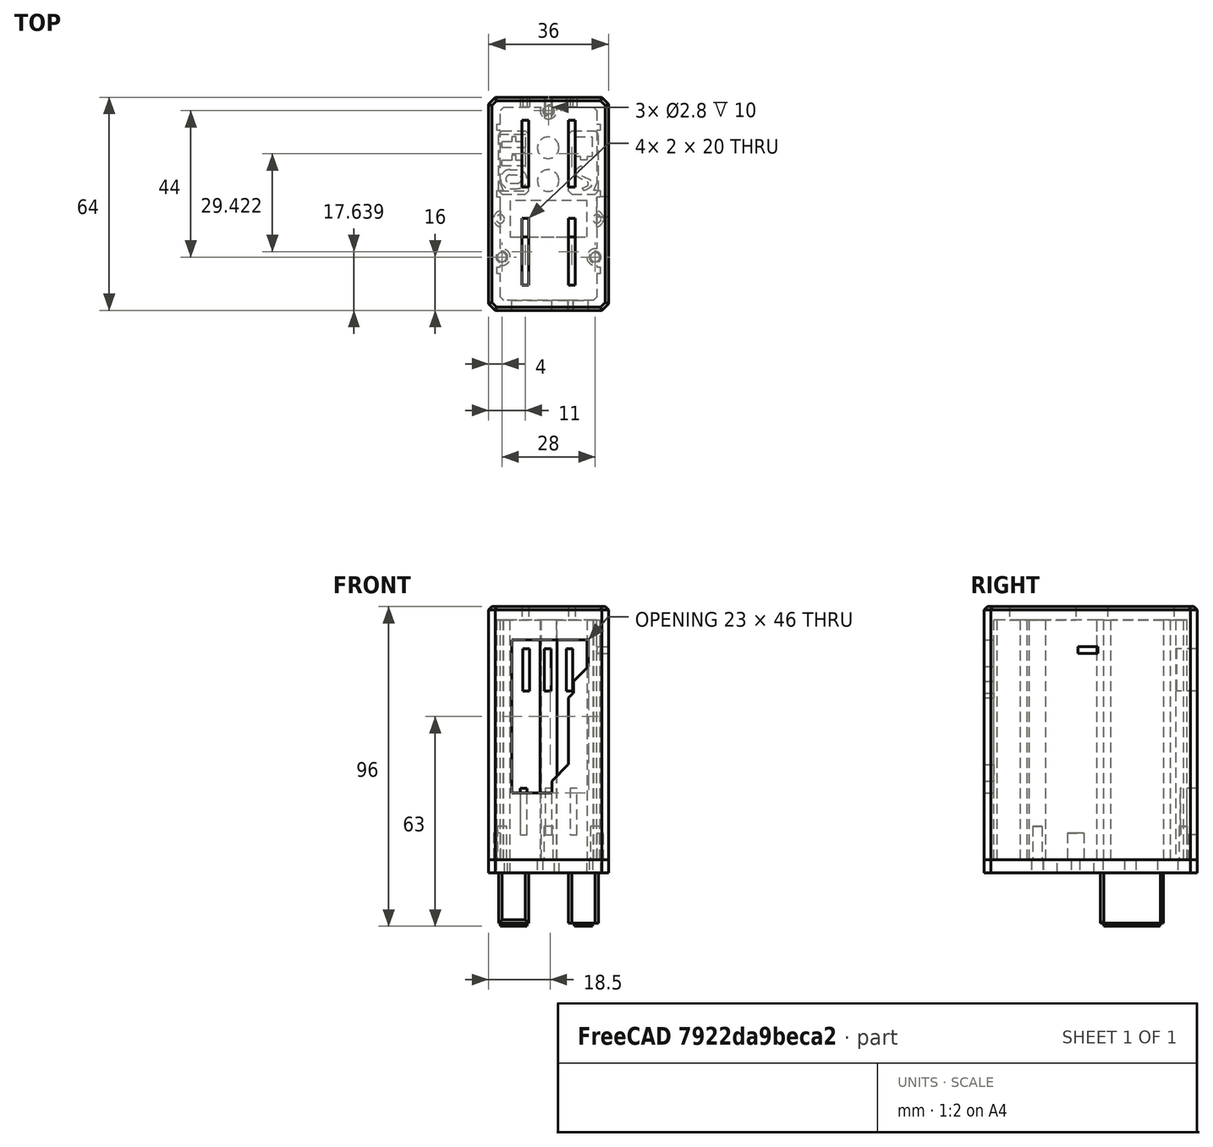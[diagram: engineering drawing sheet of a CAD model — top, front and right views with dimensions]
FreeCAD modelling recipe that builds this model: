
FCSTD DOCUMENT  (FreeCAD 0.19R)
Label: SwitchBox1
License: All rights reserved
LicenseURL: http://en.wikipedia.org/wiki/All_rights_reserved
objects: Sketcher::SketchObject×19, PartDesign::Pocket×11, PartDesign::Chamfer×9, PartDesign::Pad×8, PartDesign::Mirrored×2, PartDesign::Body×2, PartDesign::LinearPattern×1, PartDesign::Fillet×1, Mesh::Feature×1
note: 82 computed .brp shape members not serialized (recipe doc carries the construction recipe); baked Part::Feature solids carry a one-line shape summary decoded from their .brp

FEATURE [Sketcher::SketchObject] Sketch003
  FullyConstrained = true
  MapMode = 5
  Support = -> [XY_Plane001]
  sketch-geometry (4):
    g0: LineSegment StartX=-18 StartY=32 StartZ=0 EndX=18 EndY=32 EndZ=0
    g1: LineSegment StartX=18 StartY=32 StartZ=0 EndX=18 EndY=-32 EndZ=0
    g2: LineSegment StartX=18 StartY=-32 StartZ=0 EndX=-18 EndY=-32 EndZ=0
    g3: LineSegment StartX=-18 StartY=-32 StartZ=0 EndX=-18 EndY=32 EndZ=0
  constraints (10):
    c: Coincident(g0,g1)
    c: Coincident(g1,g2)
    c: Coincident(g2,g3)
    c: Coincident(g3,g0)
    c: Horizontal(g2)
    c: Vertical(g3)
    c: Distance(g0) = 36
    c: Distance(g1) = 64
    c: Symmetric(g0,g1,g-1)
    c: Symmetric(g0,g0,g-2)
FEATURE [PartDesign::Pad] Pad005
  Direction = (1,1,1)
  Length = 4
  Length2 = 100
  Profile = -> Sketch003
  Type = 0
FEATURE [Sketcher::SketchObject] Sketch005
  FullyConstrained = false
  MapMode = 5
  Placement = pos=(0,0,0) rot=(1,0,0;3.14159rad)
  Support = -> [Pad005]
  sketch-geometry (2):
    g0: Circle CenterX=-0.128096 CenterY=-16.8565 CenterZ=0 NormalX=0 NormalY=0 NormalZ=1 AngleXU=0 Radius=3.25
    g1: Circle CenterX=-0.128096 CenterY=-6.99288 CenterZ=0 NormalX=0 NormalY=0 NormalZ=1 AngleXU=0 Radius=3.25
  constraints (2):
    c: Diameter(g1) = 6.5
    c: Diameter(g0) = 6.5
FEATURE [PartDesign::Pocket] Pocket001
  BaseFeature = -> Pad005
  Length = 5
  Length2 = 100
  Profile = -> Sketch005
  Type = 0
FEATURE [Sketcher::SketchObject] Sketch006
  FullyConstrained = false
  MapMode = 5
  Placement = pos=(0,0,0) rot=(1,0,0;3.14159rad)
  Support = -> [Pocket001]
  sketch-geometry (8):
    g0: LineSegment StartX=-15 StartY=-2.91162 StartZ=0 EndX=-15 EndY=-21.9362 EndZ=0
    g1: LineSegment StartX=15 StartY=-2.91162 StartZ=0 EndX=15 EndY=-21.9362 EndZ=0
    g2: LineSegment StartX=-6 StartY=-2.91162 StartZ=0 EndX=-6 EndY=-21.9362 EndZ=0
    g3: LineSegment StartX=6 StartY=-2.91162 StartZ=0 EndX=6 EndY=-21.9362 EndZ=0
    g4: LineSegment StartX=-15 StartY=-2.91162 StartZ=0 EndX=-6 EndY=-2.91162 EndZ=0
    g5: LineSegment StartX=-15 StartY=-21.9362 StartZ=0 EndX=-6 EndY=-21.9362 EndZ=0
    g6: LineSegment StartX=6 StartY=-2.91162 StartZ=0 EndX=15 EndY=-2.91162 EndZ=0
    g7: LineSegment StartX=6 StartY=-21.9362 StartZ=0 EndX=15 EndY=-21.9362 EndZ=0
  constraints (20):
    c: Vertical(g0)
    c: Vertical(g2)
    c: Coincident(g0,g4)
    c: Coincident(g4,g2)
    c: Horizontal(g4)
    c: Coincident(g0,g5)
    c: Coincident(g5,g2)
    c: Coincident(g3,g6)
    c: Coincident(g6,g1)
    c: Coincident(g3,g7)
    c: Coincident(g7,g1)
    c: Horizontal(g7)
    c: Vertical(g1)
    c: Distance(g5) = 9
    c: Distance(g7) = 9
    c: Horizontal(g6)
    c: Horizontal(g5)
    c: Symmetric(g3,g2,g-2)
    c: Symmetric(g3,g2,g-2)
    c: DistanceX(g2) = -6
FEATURE [Sketcher::SketchObject] Sketch
  FullyConstrained = false
  MapMode = 5
  Support = -> [XY_Plane]
  sketch-geometry (36):
    g0: LineSegment StartX=-18 StartY=32 StartZ=0 EndX=18 EndY=32 EndZ=0
    g1: LineSegment StartX=18 StartY=32 StartZ=0 EndX=18 EndY=-32 EndZ=0
    g2: LineSegment StartX=18 StartY=-32 StartZ=0 EndX=-18 EndY=-32 EndZ=0
    g3: LineSegment StartX=-18 StartY=-32 StartZ=0 EndX=-18 EndY=32 EndZ=0
    g4: LineSegment StartX=14.5 StartY=29 StartZ=0 EndX=14.5 EndY=24 EndZ=0
    g5: LineSegment StartX=14.5 StartY=24 StartZ=0 EndX=15.5 EndY=24 EndZ=0
    g6: LineSegment StartX=15.5 StartY=24 StartZ=0 EndX=15.5 EndY=22 EndZ=0
    g7: LineSegment StartX=15.5 StartY=22 StartZ=0 EndX=14.5 EndY=22 EndZ=0
    g8: LineSegment StartX=14.5 StartY=22 StartZ=0 EndX=14.5 EndY=4 EndZ=0
    g9: LineSegment StartX=14.5 StartY=4 StartZ=0 EndX=15.5 EndY=4 EndZ=0
    g10: LineSegment StartX=15.5 StartY=4 StartZ=0 EndX=15.5 EndY=2 EndZ=0
    g11: LineSegment StartX=15.5 StartY=2 StartZ=0 EndX=14.5 EndY=2 EndZ=0
    g12: LineSegment StartX=14.5 StartY=2 StartZ=0 EndX=14.5 EndY=-19 EndZ=0
    g13: LineSegment StartX=14.5 StartY=-19 StartZ=0 EndX=15.5 EndY=-19 EndZ=0
    g14: LineSegment StartX=15.5 StartY=-19 StartZ=0 EndX=15.5 EndY=-21 EndZ=0
    g15: LineSegment StartX=15.5 StartY=-21 StartZ=0 EndX=14.5 EndY=-21 EndZ=0
    g16: LineSegment StartX=14.5 StartY=-21 StartZ=0 EndX=14.5 EndY=-29 EndZ=0
    g17: LineSegment StartX=14.5 StartY=-29 StartZ=0 EndX=-14.5 EndY=-29 EndZ=0
    g18: LineSegment StartX=-14.5 StartY=-21 StartZ=0 EndX=-15.5 EndY=-21 EndZ=0
    g19: LineSegment StartX=-15.5 StartY=-21 StartZ=0 EndX=-15.5 EndY=-19 EndZ=0
    g20: LineSegment StartX=-15.5 StartY=-19 StartZ=0 EndX=-14.5 EndY=-19 EndZ=0
    g21: LineSegment StartX=-14.5 StartY=-19 StartZ=0 EndX=-14.5 EndY=2 EndZ=0
    g22: LineSegment StartX=-14.5 StartY=2 StartZ=0 EndX=-15.5 EndY=2 EndZ=0
    g23: LineSegment StartX=-15.5 StartY=2 StartZ=0 EndX=-15.5 EndY=4 EndZ=0
    g24: LineSegment StartX=-15.5 StartY=4 StartZ=0 EndX=-14.5 EndY=4 EndZ=0
    g25: LineSegment StartX=-14.5 StartY=4 StartZ=0 EndX=-14.5 EndY=22 EndZ=0
    g26: LineSegment StartX=-14.5 StartY=22 StartZ=0 EndX=-15.5 EndY=22 EndZ=0
    g27: LineSegment StartX=-15.5 StartY=22 StartZ=0 EndX=-15.5 EndY=24 EndZ=0
    g28: LineSegment StartX=-15.5 StartY=24 StartZ=0 EndX=-14.5 EndY=24 EndZ=0
    g29: LineSegment StartX=-14.5 StartY=24 StartZ=0 EndX=-14.5 EndY=29 EndZ=0
    g30: LineSegment StartX=-14.5 StartY=29 StartZ=0 EndX=14.5 EndY=29 EndZ=0
    g31: LineSegment StartX=-14.5 StartY=52.6434 StartZ=0 EndX=-14.5 EndY=-62.9072 EndZ=0
    g32: LineSegment StartX=14.5 StartY=55.5069 StartZ=0 EndX=14.5 EndY=-57.6711 EndZ=0
    g33: LineSegment StartX=15.5 StartY=55.8398 StartZ=0 EndX=15.5 EndY=-58.9978 EndZ=0
    g34: LineSegment StartX=-15.5 StartY=58.5357 StartZ=0 EndX=-15.5 EndY=-69.96 EndZ=0
    g35: LineSegment StartX=-14.5 StartY=-29 StartZ=0 EndX=-14.5 EndY=-21 EndZ=0
  constraints (101):
    c: Horizontal(g0)
    c: Coincident(g0,g1)
    c: Coincident(g1,g2)
    c: Coincident(g2,g3)
    c: Coincident(g3,g0)
    c: Vertical(g4)
    c: Coincident(g4,g5)
    c: Coincident(g5,g6)
    c: Coincident(g6,g7)
    c: Horizontal(g7)
    c: Coincident(g7,g8)
    c: Vertical(g8)
    c: Coincident(g8,g9)
    c: Coincident(g9,g10)
    c: Coincident(g10,g11)
    c: Coincident(g11,g12)
    c: Vertical(g12)
    c: Coincident(g12,g13)
    c: Coincident(g13,g14)
    c: Coincident(g14,g15)
    c: Coincident(g15,g16)
    c: Coincident(g16,g17)
    c: Horizontal(g17)
    c: Coincident(g18,g19)
    c: Vertical(g19)
    c: Coincident(g19,g20)
    c: Coincident(g20,g21)
    c: Vertical(g21)
    c: Coincident(g21,g22)
    c: Coincident(g22,g23)
    c: Coincident(g23,g24)
    c: Horizontal(g24)
    c: Coincident(g24,g25)
    c: Coincident(g25,g26)
    c: Coincident(g26,g27)
    c: Vertical(g27)
    c: Coincident(g27,g28)
    c: Horizontal(g28)
    c: Coincident(g28,g29)
    c: Vertical(g29)
    c: Coincident(g29,g30)
    c: Coincident(g30,g4)
    c: Horizontal(g30)
    c: Symmetric(g1,g2,g-2)
    c: Vertical(g3)
    c: Symmetric(g7,g25,g-2)
    c: Vertical(g31)
    c: Vertical(g32)
    c: Vertical(g33)
    c: PointOnObject(g18,g31)
    c: PointOnObject(g20,g31)
    c: PointOnObject(g24,g31)
    c: PointOnObject(g25,g31)
    c: PointOnObject(g28,g31)
    c: PointOnObject(g16,g32)
    c: PointOnObject(g15,g32)
    c: PointOnObject(g12,g32)
    c: PointOnObject(g8,g32)
    c: PointOnObject(g4,g32)
    c: PointOnObject(g14,g33)
    c: PointOnObject(g13,g33)
    c: PointOnObject(g10,g33)
    c: PointOnObject(g9,g33)
    c: PointOnObject(g6,g33)
    c: PointOnObject(g5,g33)
    c: PointOnObject(g18,g34)
    c: PointOnObject(g22,g34)
    c: PointOnObject(g23,g34)
    c: PointOnObject(g26,g34)
    c: DistanceX(g34,g33) = 31
    c: Horizontal(g26)
    c: Horizontal(g13)
    c: Horizontal(g15)
    c: Horizontal(g11)
    c: Horizontal(g9)
    c: Vertical(g34)
    c: Distance(g32,g33) = 1
    c: Distance(g34,g31) = 1
    c: Coincident(g17,g35)
    c: Coincident(g35,g18)
    c: Vertical(g35)
    c: Horizontal(g20)
    c: Horizontal(g18)
    c: Equal(g14,g10)
    c: Equal(g10,g6)
    c: Equal(g6,g27)
    c: Equal(g27,g23)
    c: Equal(g23,g19)
    c: Distance(g10) = 2
    c: Distance(g28,g24) = 20
    c: Horizontal(g22)
    c: Horizontal(g5)
    c: Distance(g24,g20) = 23
    c: DistanceY(g20,g13) = 0
    c: DistanceY(g9,g24) = 0
    c: Distance(g4) = 5
    c: Distance(g0) = 36
    c: Distance(g4,g0) = 3
    c: DistanceY(g1,g16) = 3
    c: Symmetric(g1,g0,g-1)
    c: DistanceY(g1) = -32
FEATURE [PartDesign::Pad] Pad
  Direction = (1,1,1)
  Length = 72
  Length2 = 100
  Profile = -> Sketch
  Type = 0
FEATURE [Sketcher::SketchObject] Sketch002
  FullyConstrained = true
  MapMode = 5
  Placement = pos=(0,-32,0) rot=(1,0,0;1.5708rad)
  Support = -> [Pad]
  sketch-geometry (10):
    g0: LineSegment StartX=-11 StartY=66 StartZ=0 EndX=12 EndY=66 EndZ=0
    g1: LineSegment StartX=-11 StartY=20 StartZ=0 EndX=-11 EndY=66 EndZ=0
    g2: LineSegment StartX=-11 StartY=20 StartZ=0 EndX=1 EndY=20 EndZ=0
    g3: LineSegment StartX=1 StartY=20 StartZ=0 EndX=1 EndY=28.5 EndZ=0
    g4: LineSegment StartX=1 StartY=28.5 StartZ=0 EndX=6 EndY=28.5 EndZ=0
    g5: LineSegment StartX=6 StartY=28.5 StartZ=0 EndX=6 EndY=50 EndZ=0
    g6: LineSegment StartX=6 StartY=50 StartZ=0 EndX=7.5 EndY=50 EndZ=0
    g7: LineSegment StartX=7.5 StartY=50 StartZ=0 EndX=7.5 EndY=58 EndZ=0
    g8: LineSegment StartX=7.5 StartY=58 StartZ=0 EndX=12 EndY=58 EndZ=0
    g9: LineSegment StartX=12 StartY=58 StartZ=0 EndX=12 EndY=66 EndZ=0
  constraints (30):
    c: Coincident(g1,g0)
    c: Horizontal(g0)
    c: Vertical(g1)
    c: DistanceX(g1) = -11
    c: Coincident(g1,g2)
    c: Horizontal(g2)
    c: Coincident(g2,g3)
    c: Vertical(g3)
    c: Coincident(g3,g4)
    c: Coincident(g4,g5)
    c: Vertical(g5)
    c: Coincident(g5,g6)
    c: Coincident(g6,g7)
    c: Coincident(g7,g8)
    c: Horizontal(g8)
    c: Coincident(g8,g9)
    c: Vertical(g9)
    c: Coincident(g0,g9)
    c: DistanceX(g0) = 12
    c: DistanceX(g7) = 7.5
    c: DistanceX(g5) = 6
    c: Horizontal(g6)
    c: Vertical(g7)
    c: Horizontal(g4)
    c: DistanceY(g0) = 66
    c: Distance(g9) = 8
    c: Distance(g6,g0) = 16
    c: Distance(g4,g0) = 37.5
    c: Distance(g2,g0) = 46
    c: DistanceX(g2) = 1
FEATURE [PartDesign::Pocket] Pocket
  BaseFeature = -> Pad
  Length = 5
  Length2 = 100
  Profile = -> Sketch002
  Type = 0
FEATURE [Sketcher::SketchObject] Sketch013
  FullyConstrained = false
  MapMode = 5
  Placement = pos=(0,0,0) rot=(1,0,0;3.14159rad)
  sketch-geometry (5):
    g0: Circle CenterX=-14.0386 CenterY=15.9762 CenterZ=0 NormalX=0 NormalY=0 NormalZ=1 AngleXU=0 Radius=1.75
    g1: Circle CenterX=13.9774 CenterY=16.0224 CenterZ=0 NormalX=0 NormalY=0 NormalZ=1 AngleXU=0 Radius=1.75
    g2: Circle CenterX=-14.5073 CenterY=-5.11921 CenterZ=0 NormalX=0 NormalY=0 NormalZ=1 AngleXU=0 Radius=1.75
    g3: Circle CenterX=14.4969 CenterY=-5.13026 CenterZ=0 NormalX=0 NormalY=0 NormalZ=1 AngleXU=0 Radius=1.75
    g4: Circle CenterX=0 CenterY=-27.9739 CenterZ=0 NormalX=0 NormalY=0 NormalZ=1 AngleXU=0 Radius=1.75
  constraints (6):
    c: PointOnObject(g4,g-2)
    c: Diameter(g0) = 3.5
    c: Equal(g0,g1)
    c: Equal(g0,g3)
    c: Equal(g0,g2)
    c: Equal(g0,g4)
FEATURE [Sketcher::SketchObject] Sketch014
  FullyConstrained = true
  MapMode = 5
  Placement = pos=(0,0,72) rot=(0,0,1;0rad)
  sketch-geometry (4):
    g0: LineSegment StartX=-18 StartY=32 StartZ=0 EndX=18 EndY=32 EndZ=0
    g1: LineSegment StartX=18 StartY=32 StartZ=0 EndX=18 EndY=-32 EndZ=0
    g2: LineSegment StartX=18 StartY=-32 StartZ=0 EndX=-18 EndY=-32 EndZ=0
    g3: LineSegment StartX=-18 StartY=-32 StartZ=0 EndX=-18 EndY=32 EndZ=0
  constraints (10):
    c: Coincident(g0,g1)
    c: Coincident(g1,g2)
    c: Coincident(g2,g3)
    c: Coincident(g3,g0)
    c: Horizontal(g2)
    c: Vertical(g3)
    c: Symmetric(g0,g0,g-2)
    c: Distance(g0) = 36
    c: Distance(g1) = 64
    c: Symmetric(g1,g0,g-1)
FEATURE [PartDesign::Pad] Pad007
  BaseFeature = -> Pocket
  Direction = (1,1,1)
  Length = 4
  Length2 = 100
  Profile = -> Sketch014
  Type = 0
FEATURE [Sketcher::SketchObject] Sketch011
  FullyConstrained = true
  MapMode = 5
  Placement = pos=(0,0,0) rot=(1,0,0;3.14159rad)
  Support = -> [Pad007]
  sketch-geometry (6):
    g0: Circle CenterX=-12 CenterY=-5.1 CenterZ=0 NormalX=0 NormalY=0 NormalZ=1 AngleXU=0 Radius=2.5
    g1: Circle CenterX=12 CenterY=-5.1 CenterZ=0 NormalX=0 NormalY=0 NormalZ=1 AngleXU=0 Radius=2.5
    g2: Circle CenterX=-14 CenterY=16 CenterZ=0 NormalX=0 NormalY=0 NormalZ=1 AngleXU=0 Radius=2.5
    g3: Circle CenterX=14 CenterY=16 CenterZ=0 NormalX=0 NormalY=0 NormalZ=1 AngleXU=0 Radius=2.5
    g4: Circle CenterX=0 CenterY=29 CenterZ=0 NormalX=0 NormalY=0 NormalZ=1 AngleXU=0 Radius=2.5
    g5: Circle CenterX=0 CenterY=-28 CenterZ=0 NormalX=0 NormalY=0 NormalZ=1 AngleXU=0 Radius=2.5
  constraints (16):
    c: Diameter(g3) = 5
    c: Equal(g3,g2)
    c: Equal(g3,g1)
    c: Equal(g3,g0)
    c: Symmetric(g1,g0,g-2)
    c: Symmetric(g3,g2,g-2)
    c: DistanceX(g1) = 12
    c: DistanceX(g3) = 14
    c: PointOnObject(g4,g-2)
    c: Diameter(g4) = 5
    c: DistanceY(g4) = 29
    c: DistanceY(g1) = -5.1
    c: DistanceY(g3) = 16
    c: PointOnObject(g5,g-2)
    c: Diameter(g5) = 5
    c: DistanceY(g5) = -28
FEATURE [PartDesign::Pad] Pad008
  BaseFeature = -> Pad007
  Direction = (1,1,1)
  Length = 73
  Length2 = 100
  Profile = -> Sketch011
  Reversed = true
  Type = 0
FEATURE [Sketcher::SketchObject] Sketch015
  FullyConstrained = true
  MapMode = 5
  Placement = pos=(0,0,0) rot=(1,0,0;3.14159rad)
  Support = -> [Pad008]
  sketch-geometry (3):
    g0: Circle CenterX=-14 CenterY=16 CenterZ=0 NormalX=0 NormalY=0 NormalZ=1 AngleXU=0 Radius=1.4
    g1: Circle CenterX=14 CenterY=16 CenterZ=0 NormalX=0 NormalY=0 NormalZ=1 AngleXU=0 Radius=1.4
    g2: Circle CenterX=0 CenterY=-28 CenterZ=0 NormalX=0 NormalY=0 NormalZ=1 AngleXU=0 Radius=1.4
  constraints (8):
    c: Diameter(g1) = 2.8
    c: Equal(g1,g0)
    c: Equal(g1,g2)
    c: Symmetric(g0,g1,g-2)
    c: PointOnObject(g2,g-2)
    c: DistanceY(g2) = -28
    c: DistanceX(g1) = 14
    c: DistanceY(g1) = 16
FEATURE [PartDesign::Pocket] Pocket002
  BaseFeature = -> Pad008
  Length = 10
  Length2 = 100
  Profile = -> Sketch015
  Type = 0
FEATURE [Sketcher::SketchObject] Sketch016
  FullyConstrained = true
  MapMode = 5
  Placement = pos=(0,0,0) rot=(1,0,0;3.14159rad)
  sketch-geometry (6):
    g0: LineSegment StartX=-11.5 StartY=10 StartZ=0 EndX=11.5 EndY=10 EndZ=0
    g1: LineSegment StartX=11.5 StartY=10 StartZ=0 EndX=11.5 EndY=-1 EndZ=0
    g2: LineSegment StartX=11.5 StartY=-1 StartZ=0 EndX=-11.5 EndY=-1 EndZ=0
    g3: LineSegment StartX=-11.5 StartY=-1 StartZ=0 EndX=-11.5 EndY=10 EndZ=0
    g4: Circle CenterX=-14.5 CenterY=4.5 CenterZ=0 NormalX=0 NormalY=0 NormalZ=1 AngleXU=0 Radius=1.25
    g5: Circle CenterX=14.5 CenterY=4.5 CenterZ=0 NormalX=0 NormalY=0 NormalZ=1 AngleXU=0 Radius=1.25
  constraints (16):
    c: Coincident(g0,g1)
    c: Coincident(g1,g2)
    c: Coincident(g2,g3)
    c: Coincident(g3,g0)
    c: Horizontal(g2)
    c: Vertical(g1)
    c: Vertical(g3)
    c: Distance(g0) = 23
    c: Distance(g1) = 11
    c: Symmetric(g0,g0,g-2)
    c: DistanceY(g0) = 10
    c: Diameter(g5) = 2.5
    c: Equal(g5,g4)
    c: Distance(g5,g4) = 29
    c: Symmetric(g5,g4,g-2)
    c: DistanceY(g5) = 4.5
FEATURE [PartDesign::Pocket] Pocket003
  BaseFeature = -> Pocket001
  Length = 5
  Length2 = 100
  Profile = -> Sketch016
  Type = 0
FEATURE [PartDesign::Pocket] Pocket004
  BaseFeature = -> Pocket003
  Length = 5
  Length2 = 100
  Profile = -> Sketch013
  Type = 0
FEATURE [Sketcher::SketchObject] Sketch018
  FullyConstrained = true
  MapMode = 5
  Placement = pos=(0,0,0) rot=(1,0,0;3.14159rad)
  Support = -> [Pocket002]
  sketch-geometry (2):
    g0: Circle CenterX=-14 CenterY=4.5 CenterZ=0 NormalX=0 NormalY=0 NormalZ=1 AngleXU=0 Radius=2.5
    g1: Circle CenterX=14 CenterY=4.5 CenterZ=0 NormalX=0 NormalY=0 NormalZ=1 AngleXU=0 Radius=2.5
  constraints (5):
    c: DistanceY(g1) = 4.5
    c: Symmetric(g1,g0,g-2)
    c: Diameter(g1) = 5
    c: Diameter(g0) = 5
    c: DistanceX(g1) = 14
FEATURE [PartDesign::Pocket] Pocket005
  BaseFeature = -> Pocket002
  Length = 8
  Length2 = 100
  Profile = -> Sketch018
  Type = 0
FEATURE [PartDesign::Chamfer] Chamfer003
  Angle = 45
  Base = -> Pocket005 [Edge2,Edge1,Edge8,Edge5]
  BaseFeature = -> Pocket005
  ChamferType = 0
  FlipDirection = false
  Size = 2
  Size2 = 1
  SupportTransform = false
FEATURE [PartDesign::Chamfer] Chamfer004
  Angle = 45
  Base = -> Chamfer003 [Edge84,Edge80,Edge127,Edge124]
  BaseFeature = -> Chamfer003
  ChamferType = 0
  FlipDirection = false
  Size = 1
  Size2 = 1
  SupportTransform = false
FEATURE [PartDesign::Chamfer] Chamfer005
  Angle = 45
  Base = -> Chamfer004 [Face86]
  BaseFeature = -> Chamfer004
  ChamferType = 0
  FlipDirection = false
  Size = 1
  Size2 = 1
  SupportTransform = false
FEATURE [Sketcher::SketchObject] Sketch019
  FullyConstrained = false
  MapMode = 5
  Placement = pos=(0,32,0) rot=(0,0.707107,0.707107;3.14159rad)
  Support = -> [Chamfer005]
  sketch-geometry (4):
    g0: LineSegment StartX=-7.28516 StartY=63.2989 StartZ=0 EndX=-5.28516 EndY=63.2989 EndZ=0
    g1: LineSegment StartX=-5.28516 StartY=63.2989 StartZ=0 EndX=-5.28516 EndY=50.6192 EndZ=0
    g2: LineSegment StartX=-5.28516 StartY=50.6192 StartZ=0 EndX=-7.28516 EndY=50.6192 EndZ=0
    g3: LineSegment StartX=-7.28516 StartY=50.6192 StartZ=0 EndX=-7.28516 EndY=63.2989 EndZ=0
  constraints (9):
    c: Coincident(g0,g1)
    c: Coincident(g1,g2)
    c: Coincident(g2,g3)
    c: Coincident(g3,g0)
    c: Horizontal(g0)
    c: Horizontal(g2)
    c: Vertical(g1)
    c: Vertical(g3)
    c: Distance(g0) = 2
FEATURE [PartDesign::Pocket] Pocket006
  BaseFeature = -> Chamfer005
  Length = 11
  Length2 = 100
  Profile = -> Sketch019
  Type = 0
FEATURE [PartDesign::LinearPattern] LinearPattern
  BaseFeature = -> Pocket006
  Direction = -> Sketch019 [H_Axis]
  Length = 13
  Occurrences = 3
  Originals = -> [Pocket006]
FEATURE [Sketcher::SketchObject] Sketch020
  FullyConstrained = false
  MapMode = 5
  Placement = pos=(0,0,76) rot=(0,0,1;0rad)
  Support = -> [LinearPattern]
  sketch-geometry (4):
    g0: LineSegment StartX=-6 StartY=25.0609 StartZ=0 EndX=-8 EndY=25.0609 EndZ=0
    g1: LineSegment StartX=-8 StartY=25.0609 StartZ=0 EndX=-8 EndY=5.06087 EndZ=0
    g2: LineSegment StartX=-8 StartY=5.06087 StartZ=0 EndX=-6 EndY=5.06087 EndZ=0
    g3: LineSegment StartX=-6 StartY=5.06087 StartZ=0 EndX=-6 EndY=25.0609 EndZ=0
  constraints (11):
    c: Coincident(g0,g1)
    c: Coincident(g1,g2)
    c: Coincident(g2,g3)
    c: Coincident(g3,g0)
    c: Horizontal(g0)
    c: Horizontal(g2)
    c: Vertical(g1)
    c: Vertical(g3)
    c: Distance(g1) = 20
    c: Distance(g0) = 2
    c: DistanceX(g0) = -8
FEATURE [PartDesign::Pocket] Pocket007
  BaseFeature = -> LinearPattern
  Length = 5
  Length2 = 100
  Profile = -> Sketch020
  Type = 0
FEATURE [PartDesign::Mirrored] Mirrored
  BaseFeature = -> Pocket007
  MirrorPlane = -> Sketch020 [V_Axis]
  Originals = -> [Pocket007]
FEATURE [Sketcher::SketchObject] Sketch021
  FullyConstrained = false
  MapMode = 5
  Placement = pos=(0,32,0) rot=(0,0.707107,0.707107;3.14159rad)
  Support = -> [Mirrored]
  sketch-geometry (12):
    g0: LineSegment StartX=-8.45169 StartY=21.5064 StartZ=0 EndX=-6.45169 EndY=21.5064 EndZ=0
    g1: LineSegment StartX=-6.45169 StartY=21.5064 StartZ=0 EndX=-6.45169 EndY=7.50641 EndZ=0
    g2: LineSegment StartX=-6.45169 StartY=7.50641 StartZ=0 EndX=-8.45169 EndY=7.50641 EndZ=0
    g3: LineSegment StartX=-8.45169 StartY=7.50641 StartZ=0 EndX=-8.45169 EndY=21.5064 EndZ=0
    g4: LineSegment StartX=6.45169 StartY=21.5064 StartZ=0 EndX=8.45169 EndY=21.5064 EndZ=0
    g5: LineSegment StartX=8.45169 StartY=21.5064 StartZ=0 EndX=8.45169 EndY=7.50641 EndZ=0
    g6: LineSegment StartX=8.45169 StartY=7.50641 StartZ=0 EndX=6.45169 EndY=7.50641 EndZ=0
    g7: LineSegment StartX=6.45169 StartY=7.50641 StartZ=0 EndX=6.45169 EndY=21.5064 EndZ=0
    g8: LineSegment StartX=-1.04536 StartY=21.5013 StartZ=0 EndX=0.954643 EndY=21.5013 EndZ=0
    g9: LineSegment StartX=0.954643 StartY=21.5013 StartZ=0 EndX=0.954643 EndY=7.50135 EndZ=0
    g10: LineSegment StartX=0.954643 StartY=7.50135 StartZ=0 EndX=-1.04536 EndY=7.50135 EndZ=0
    g11: LineSegment StartX=-1.04536 StartY=7.50135 StartZ=0 EndX=-1.04536 EndY=21.5013 EndZ=0
  constraints (31):
    c: Coincident(g0,g1)
    c: Coincident(g1,g2)
    c: Coincident(g2,g3)
    c: Coincident(g3,g0)
    c: Horizontal(g0)
    c: Horizontal(g2)
    c: Vertical(g1)
    c: Vertical(g3)
    c: Coincident(g4,g5)
    c: Coincident(g5,g6)
    c: Coincident(g6,g7)
    c: Coincident(g7,g4)
    c: Horizontal(g4)
    c: Horizontal(g6)
    c: Vertical(g5)
    c: Vertical(g7)
    c: Symmetric(g4,g0,g-2)
    c: Equal(g0,g4)
    c: Distance(g7) = 14
    c: Distance(g4) = 2
    c: Coincident(g8,g9)
    c: Coincident(g9,g10)
    c: Coincident(g10,g11)
    c: Coincident(g11,g8)
    c: Horizontal(g8)
    c: Horizontal(g10)
    c: Vertical(g9)
    c: Vertical(g11)
    c: Distance(g10) = 2
    c: Distance(g11) = 14
    c: Distance(g1) = 14
FEATURE [PartDesign::Pocket] Pocket008
  BaseFeature = -> Mirrored
  Length = 5
  Length2 = 100
  Profile = -> Sketch021
  Type = 0
FEATURE [Sketcher::SketchObject] Sketch022
  FullyConstrained = false
  MapMode = 5
  Placement = pos=(0,0,76) rot=(0,0,1;0rad)
  Support = -> [Pocket008]
  sketch-geometry (8):
    g0: LineSegment StartX=-6 StartY=-4.3614 StartZ=0 EndX=-8 EndY=-4.3614 EndZ=0
    g1: LineSegment StartX=-8 StartY=-4.3614 StartZ=0 EndX=-8 EndY=-24.3614 EndZ=0
    g2: LineSegment StartX=-8 StartY=-24.3614 StartZ=0 EndX=-6 EndY=-24.3614 EndZ=0
    g3: LineSegment StartX=-6 StartY=-24.3614 StartZ=0 EndX=-6 EndY=-4.3614 EndZ=0
    g4: LineSegment StartX=8 StartY=-4.3614 StartZ=0 EndX=6 EndY=-4.3614 EndZ=0
    g5: LineSegment StartX=6 StartY=-4.3614 StartZ=0 EndX=6 EndY=-24.3614 EndZ=0
    g6: LineSegment StartX=6 StartY=-24.3614 StartZ=0 EndX=8 EndY=-24.3614 EndZ=0
    g7: LineSegment StartX=8 StartY=-24.3614 StartZ=0 EndX=8 EndY=-4.3614 EndZ=0
  constraints (22):
    c: Coincident(g0,g1)
    c: Coincident(g1,g2)
    c: Coincident(g2,g3)
    c: Coincident(g3,g0)
    c: Horizontal(g0)
    c: Horizontal(g2)
    c: Vertical(g1)
    c: Vertical(g3)
    c: Coincident(g4,g5)
    c: Coincident(g5,g6)
    c: Coincident(g6,g7)
    c: Coincident(g7,g4)
    c: Horizontal(g4)
    c: Horizontal(g6)
    c: Vertical(g5)
    c: Vertical(g7)
    c: Equal(g4,g0)
    c: Distance(g4) = 2
    c: Symmetric(g0,g4,g-2)
    c: Equal(g1,g7)
    c: Distance(g4,g0) = 16
    c: Distance(g1) = 20
FEATURE [PartDesign::Pocket] Pocket009
  BaseFeature = -> Pocket008
  Length = 5
  Length2 = 100
  Profile = -> Sketch022
  Type = 0
FEATURE [PartDesign::Pad] Pad009
  BaseFeature = -> Pocket004
  Direction = (1,1,1)
  Length = 15
  Length2 = 100
  Profile = -> Sketch006
  Type = 0
FEATURE [Sketcher::SketchObject] Sketch017
  FullyConstrained = false
  MapMode = 5
  Placement = pos=(0,0,-15) rot=(1,0,0;3.14159rad)
  Support = -> [Pad009]
  sketch-geometry (25):
    g0: LineSegment StartX=8.09603 StartY=-14.1657 StartZ=0 EndX=8.09603 EndY=-20.1657 EndZ=0
    g1: LineSegment StartX=8.09603 StartY=-20.1657 StartZ=0 EndX=13.096 EndY=-20.1657 EndZ=0
    g2: LineSegment StartX=13.096 StartY=-20.1657 StartZ=0 EndX=13.096 EndY=-14.1657 EndZ=0
    g3: LineSegment StartX=13.096 StartY=-14.1657 StartZ=0 EndX=11.596 EndY=-14.1657 EndZ=0
    g4: LineSegment StartX=11.596 StartY=-14.1657 StartZ=0 EndX=11.596 EndY=-13.1657 EndZ=0
    g5: LineSegment StartX=11.596 StartY=-13.1657 StartZ=0 EndX=9.59603 EndY=-13.1657 EndZ=0
    g6: LineSegment StartX=9.59603 StartY=-13.1657 StartZ=0 EndX=9.59603 EndY=-14.1657 EndZ=0
    g7: LineSegment StartX=9.59603 StartY=-14.1657 StartZ=0 EndX=8.09603 EndY=-14.1657 EndZ=0
    g8-g11: Circle x4 (B-spline internal-alignment scaffolding for g12; pole/knot coordinates omitted)
    g12: BSplineCurve PolesCount=4 KnotsCount=2 Degree=3 IsPeriodic=0
    g13: GeomPoint X=10.6286 Y=-3.99416 Z=0
    g14: GeomPoint X=10.1786 Y=-10.769 Z=0
    g15-g18: Circle x4 (B-spline internal-alignment scaffolding for g19; pole/knot coordinates omitted)
    g19: BSplineCurve PolesCount=4 KnotsCount=2 Degree=3 IsPeriodic=0
    g20: GeomPoint X=10.1786 Y=-4.77358 Z=0
    g21: GeomPoint X=9.72858 Y=-11.5485 Z=0
    g22: LineSegment StartX=10.1786 StartY=-1.91539 StartZ=0 EndX=10.1786 EndY=-22.783 EndZ=0
    g23: LineSegment StartX=9.72858 StartY=-11.5485 StartZ=0 EndX=10.1786 EndY=-10.769 EndZ=0
    g24: LineSegment StartX=10.6286 StartY=-3.99416 StartZ=0 EndX=10.1786 EndY=-4.77358 EndZ=0
  constraints (49):
    c: Vertical(g0)
    c: Coincident(g0,g1)
    c: Horizontal(g1)
    c: Coincident(g1,g2)
    c: Vertical(g2)
    c: Coincident(g2,g3)
    c: Horizontal(g3)
    c: Coincident(g3,g4)
    c: Coincident(g4,g5)
    c: Horizontal(g5)
    c: Coincident(g5,g6)
    c: Coincident(g6,g7)
    c: Coincident(g7,g0)
    c: Horizontal(g7)
    c: Vertical(g4)
    c: Vertical(g6)
    c: Equal(g3,g7)
    c: Equal(g4,g6)
    c: Distance(g5) = 2
    c: Distance(g4) = 1
    c: Distance(g3) = 1.5
    c: Distance(g2) = 6
    c: Weight(g8) = 1
    c: Equal(g8,g9)
    c: Equal(g8,g10)
    c: Equal(g8,g11)
    c: InternalAlignment(g8-g11 -> g12) x4
    c: InternalAlignment(g13,g12)
    c: InternalAlignment(g14,g12)
    c: Weight(g15) = 1
    c: Equal(g15,g16)
    c: Equal(g15,g17)
    c: Equal(g15,g18)
    c: InternalAlignment(g15-g18 -> g19) x4
    c: InternalAlignment(g20,g19)
    c: InternalAlignment(g21,g19)
    c: Distance(g19,g12) = 0.9
    c: Distance(g19,g12) = 0.9
    c: Vertical(g22)
    c: PointOnObject(g19,g22)
    c: PointOnObject(g12,g22)
    c: Coincident(g23,g19)
    c: Coincident(g23,g12)
    c: Coincident(g24,g12)
    c: Coincident(g24,g19)
    c: DistanceY(g10,g9) = 0
    c: DistanceY(g17,g16) = 0
    c: Angle(g24) = -2.0944
    c: Angle(g23) = 1.0472
FEATURE [Sketcher::SketchObject] Sketch023
  FullyConstrained = false
  MapMode = 5
  Placement = pos=(0,0,-15) rot=(1,0,0;3.14159rad)
  sketch-geometry (28):
    g0: LineSegment StartX=-14.1286 StartY=-11.4813 StartZ=0 EndX=-6.82862 EndY=-11.4813 EndZ=0
    g1: LineSegment StartX=-6.82862 StartY=-11.4813 StartZ=0 EndX=-6.82862 EndY=-15.2813 EndZ=0
    g2: LineSegment StartX=-6.82862 StartY=-15.2813 StartZ=0 EndX=-8.02862 EndY=-15.2813 EndZ=0
    g3: LineSegment StartX=-8.02862 StartY=-15.2813 StartZ=0 EndX=-8.02862 EndY=-13.0813 EndZ=0
    g4: LineSegment StartX=-8.02862 StartY=-13.0813 StartZ=0 EndX=-9.82862 EndY=-13.0813 EndZ=0
    g5: LineSegment StartX=-9.82862 StartY=-13.0813 StartZ=0 EndX=-9.82862 EndY=-14.5813 EndZ=0
    g6: LineSegment StartX=-9.82862 StartY=-14.5813 StartZ=0 EndX=-11.0286 EndY=-14.5813 EndZ=0
    g7: LineSegment StartX=-11.0286 StartY=-14.5813 StartZ=0 EndX=-11.0286 EndY=-13.0813 EndZ=0
    g8: LineSegment StartX=-11.0286 StartY=-13.0813 StartZ=0 EndX=-14.1286 EndY=-13.0813 EndZ=0
    g9: LineSegment StartX=-14.1286 StartY=-13.0813 StartZ=0 EndX=-14.1286 EndY=-11.4813 EndZ=0
    g10: LineSegment StartX=-14.1286 StartY=-17.0432 StartZ=0 EndX=-6.82862 EndY=-17.0432 EndZ=0
    g11: LineSegment StartX=-6.82862 StartY=-17.0432 StartZ=0 EndX=-6.82862 EndY=-20.8432 EndZ=0
    g12: LineSegment StartX=-6.82862 StartY=-20.8432 StartZ=0 EndX=-8.02862 EndY=-20.8432 EndZ=0
    g13: LineSegment StartX=-8.02862 StartY=-20.8432 StartZ=0 EndX=-8.02862 EndY=-18.6432 EndZ=0
    g14: LineSegment StartX=-8.02862 StartY=-18.6432 StartZ=0 EndX=-9.82862 EndY=-18.6432 EndZ=0
    g15: LineSegment StartX=-9.82862 StartY=-18.6432 StartZ=0 EndX=-9.82862 EndY=-20.1432 EndZ=0
    g16: LineSegment StartX=-9.82862 StartY=-20.1432 StartZ=0 EndX=-11.0286 EndY=-20.1432 EndZ=0
    g17: LineSegment StartX=-11.0286 StartY=-20.1432 StartZ=0 EndX=-11.0286 EndY=-18.6432 EndZ=0
    g18: LineSegment StartX=-11.0286 StartY=-18.6432 StartZ=0 EndX=-14.1286 EndY=-18.6432 EndZ=0
    g19: LineSegment StartX=-14.1286 StartY=-18.6432 StartZ=0 EndX=-14.1286 EndY=-17.0432 EndZ=0
    g20: ArcOfCircle CenterX=-11.5677 CenterY=-7.44256 CenterZ=0 NormalX=0 NormalY=0 NormalZ=1 AngleXU=0 Radius=2.85 StartAngle=1.5708 EndAngle=4.71239
    g21: ArcOfCircle CenterX=-9.36769 CenterY=-7.44256 CenterZ=0 NormalX=0 NormalY=0 NormalZ=1 AngleXU=0 Radius=2.85 StartAngle=4.71239 EndAngle=7.85398
    g22: LineSegment StartX=-11.5677 StartY=-10.2926 StartZ=0 EndX=-9.36769 EndY=-10.2926 EndZ=0
    g23: LineSegment StartX=-11.5677 StartY=-4.59256 StartZ=0 EndX=-9.36769 EndY=-4.59256 EndZ=0
    g24: ArcOfCircle CenterX=-11.5677 CenterY=-7.44256 CenterZ=0 NormalX=0 NormalY=0 NormalZ=1 AngleXU=0 Radius=1.25 StartAngle=1.5708 EndAngle=4.71239
    g25: ArcOfCircle CenterX=-9.36769 CenterY=-7.44256 CenterZ=0 NormalX=0 NormalY=0 NormalZ=1 AngleXU=0 Radius=1.25 StartAngle=4.71239 EndAngle=7.85398
    g26: LineSegment StartX=-11.5677 StartY=-8.69256 StartZ=0 EndX=-9.36769 EndY=-8.69256 EndZ=0
    g27: LineSegment StartX=-11.5677 StartY=-6.19256 StartZ=0 EndX=-9.36769 EndY=-6.19256 EndZ=0
  constraints (74):
    c: Horizontal(g0)
    c: Coincident(g0,g1)
    c: Vertical(g1)
    c: Coincident(g1,g2)
    c: Coincident(g2,g3)
    c: Coincident(g3,g4)
    c: Horizontal(g4)
    c: Coincident(g4,g5)
    c: Vertical(g5)
    c: Coincident(g5,g6)
    c: Coincident(g6,g7)
    c: Coincident(g7,g8)
    c: Coincident(g8,g9)
    c: Coincident(g9,g0)
    c: Horizontal(g10)
    c: Coincident(g10,g11)
    c: Vertical(g11)
    c: Coincident(g11,g12)
    c: Coincident(g12,g13)
    c: Vertical(g13)
    c: Coincident(g13,g14)
    c: Horizontal(g14)
    c: Coincident(g14,g15)
    c: Vertical(g15)
    c: Coincident(g15,g16)
    c: Horizontal(g16)
    c: Coincident(g16,g17)
    c: Coincident(g17,g18)
    c: Coincident(g18,g19)
    c: Coincident(g19,g10)
    c: Vertical(g19)
    c: Equal(g10,g0)
    c: Equal(g11,g1)
    c: Equal(g19,g9)
    c: Equal(g7,g17)
    c: Equal(g14,g4)
    c: Equal(g12,g2)
    c: Horizontal(g6)
    c: Horizontal(g2)
    c: Vertical(g7)
    c: Vertical(g9)
    c: Horizontal(g18)
    c: Vertical(g17)
    c: Horizontal(g8)
    c: Vertical(g3)
    c: Horizontal(g12)
    c: Distance(g9) = 1.6
    c: Distance(g14,g10) = 1.6
    c: Distance(g4,g0) = 1.6
    c: Distance(g16) = 1.2
    c: Distance(g12) = 1.2
    c: Distance(g15) = 1.5
    c: Distance(g0) = 7.3
    c: Equal(g6,g16)
    c: Distance(g4) = 1.8
    c: Distance(g1) = 3.8
    c: DistanceX(g8,g10) = 0
    c: Tangent(g20,g23) = 1.5708
    c: Tangent(g20,g22) = -1.5708
    c: Tangent(g22,g21) = -1.5708
    c: Tangent(g23,g21) = 1.5708
    c: Horizontal(g22)
    c: Equal(g20,g21)
    c: Tangent(g24,g27) = 1.5708
    c: Tangent(g24,g26) = -1.5708
    c: Tangent(g26,g25) = -1.5708
    c: Tangent(g27,g25) = 1.5708
    c: Horizontal(g26)
    c: Equal(g24,g25)
    c: Coincident(g24,g20)
    c: Equal(g23,g27)
    c: Distance(g25,g21) = 1.6
    c: Distance(g27) = 2.2
    c: Diameter(g21) = 5.7
FEATURE [Sketcher::SketchObject] Sketch024
  FullyConstrained = false
  MapMode = 5
  Placement = pos=(0,0,0) rot=(1,0,0;3.14159rad)
  Support = -> [Pocket009]
  sketch-geometry (3):
    g0: LineSegment StartX=-14.9852 StartY=-4 StartZ=0 EndX=-13.563 EndY=-4 EndZ=0
    g1: LineSegment StartX=-13.563 StartY=-4 StartZ=0 EndX=-15.1748 EndY=-7.73851 EndZ=0
    g2: LineSegment StartX=-15.1748 StartY=-7.73851 StartZ=0 EndX=-14.9852 EndY=-4 EndZ=0
  constraints (5):
    c: Horizontal(g0)
    c: Coincident(g0,g1)
    c: Coincident(g1,g2)
    c: Coincident(g2,g0)
    c: DistanceY(g0) = -4
FEATURE [PartDesign::Pad] Pad012
  BaseFeature = -> Pocket009
  Direction = (1,1,1)
  Length = 75
  Length2 = 100
  Profile = -> Sketch024
  Reversed = true
  Type = 0
FEATURE [PartDesign::Mirrored] Mirrored001
  BaseFeature = -> Pad012
  MirrorPlane = -> Sketch024 [V_Axis]
  Originals = -> [Pad012]
FEATURE [Sketcher::SketchObject] Sketch025
  ExternalGeometry = -> [Mirrored001]
  FullyConstrained = false
  MapMode = 5
  Placement = pos=(14.5,0,0) rot=(0.57735,-0.57735,-0.57735;2.0944rad)
  Support = -> [Mirrored001]
  sketch-geometry (4):
    g0: LineSegment StartX=-2.19364 StartY=64 StartZ=0 EndX=3.80636 EndY=64 EndZ=0
    g1: LineSegment StartX=3.80636 StartY=64 StartZ=0 EndX=3.80636 EndY=62 EndZ=0
    g2: LineSegment StartX=3.80636 StartY=62 StartZ=0 EndX=-2.19364 EndY=62 EndZ=0
    g3: LineSegment StartX=-2.19364 StartY=62 StartZ=0 EndX=-2.19364 EndY=64 EndZ=0
  constraints (11):
    c: Coincident(g0,g1)
    c: Coincident(g1,g2)
    c: Coincident(g2,g3)
    c: Coincident(g3,g0)
    c: Horizontal(g0)
    c: Horizontal(g2)
    c: Vertical(g1)
    c: Vertical(g3)
    c: Distance(g0) = 6
    c: Distance(g1) = 2
    c: Distance(g0,g-3) = 8
FEATURE [PartDesign::Pocket] Pocket010
  BaseFeature = -> Mirrored001
  Length = 5
  Length2 = 100
  Profile = -> Sketch025
  Type = 1
FEATURE [PartDesign::Chamfer] Chamfer008
  Angle = 45
  Base = -> Pocket010 [Edge398]
  BaseFeature = -> Pocket010
  ChamferType = 0
  FlipDirection = false
  Size = 4.4
  Size2 = 1
  SupportTransform = false
FEATURE [PartDesign::Chamfer] Chamfer009
  Angle = 45
  Base = -> Chamfer008 [Edge22]
  BaseFeature = -> Chamfer008
  ChamferType = 0
  FlipDirection = false
  Size = 1.4
  Size2 = 1
  SupportTransform = false
FEATURE [PartDesign::Chamfer] Chamfer010
  Angle = 45
  Base = -> Chamfer009 [Edge29]
  BaseFeature = -> Chamfer009
  ChamferType = 0
  FlipDirection = false
  Size = 4.9
  Size2 = 1
  SupportTransform = false
FEATURE [PartDesign::Body] Body
  Group = -> [Sketch,Pad,Sketch002,Pocket,Sketch011,Sketch014,Pad007,Pad008,Sketch015,Pocket002,Sketch018,Pocket005,Chamfer003,Chamfer004,Chamfer005,Sketch019,Pocket006,LinearPattern,Sketch020,Pocket007,Mirrored,Sketch021,Pocket008,Sketch022,Pocket009,Sketch024,Pad012,Mirrored001,Sketch025,Pocket010,Chamfer008,Chamfer009,Chamfer010]
  Origin = -> Origin
  Tip = -> Chamfer010
FEATURE [PartDesign::Pad] Pad013
  BaseFeature = -> Pad009
  Direction = (1,1,1)
  Length = 1
  Length2 = 100
  Profile = -> Sketch017
  Type = 0
FEATURE [PartDesign::Pad] Pad014
  BaseFeature = -> Pad013
  Direction = (1,1,1)
  Length = 1
  Length2 = 100
  Profile = -> Sketch023
  Type = 0
FEATURE [PartDesign::Fillet] Fillet
  Base = -> Pad014 [Edge61,Edge56,Edge57,Edge59,Edge46,Edge48,Edge50,Edge45]
  BaseFeature = -> Pad014
  Radius = 2
  SupportTransform = false
FEATURE [PartDesign::Chamfer] Chamfer
  Angle = 45
  Base = -> Fillet [Edge6]
  BaseFeature = -> Fillet
  ChamferType = 0
  FlipDirection = false
  Size = 1
  Size2 = 1
  SupportTransform = false
FEATURE [PartDesign::Chamfer] Chamfer011
  Angle = 45
  Base = -> Chamfer [Edge23]
  BaseFeature = -> Chamfer
  ChamferType = 0
  FlipDirection = false
  Size = 1
  Size2 = 1
  SupportTransform = false
FEATURE [PartDesign::Chamfer] Chamfer012
  Angle = 45
  Base = -> Chamfer011 [Edge65,Edge67,Edge62,Edge63]
  BaseFeature = -> Chamfer011
  ChamferType = 0
  FlipDirection = false
  Size = 2
  Size2 = 1
  SupportTransform = false
FEATURE [PartDesign::Body] Body001  label="SwitchCap"
  Group = -> [Sketch003,Sketch005,Sketch006,Pad005,Pocket001,Sketch013,Sketch016,Pocket003,Pocket004,Sketch017,Pad009,Sketch023,Pad013,Pad014,Fillet,Chamfer,Chamfer011,Chamfer012]
  Origin = -> Origin001
  Placement = pos=(0,0,-4) rot=(0,0,1;0rad)
  Tip = -> Chamfer012
FEATURE [Mesh::Feature] Mesh  label="Chamfer012 (Meshed)"
